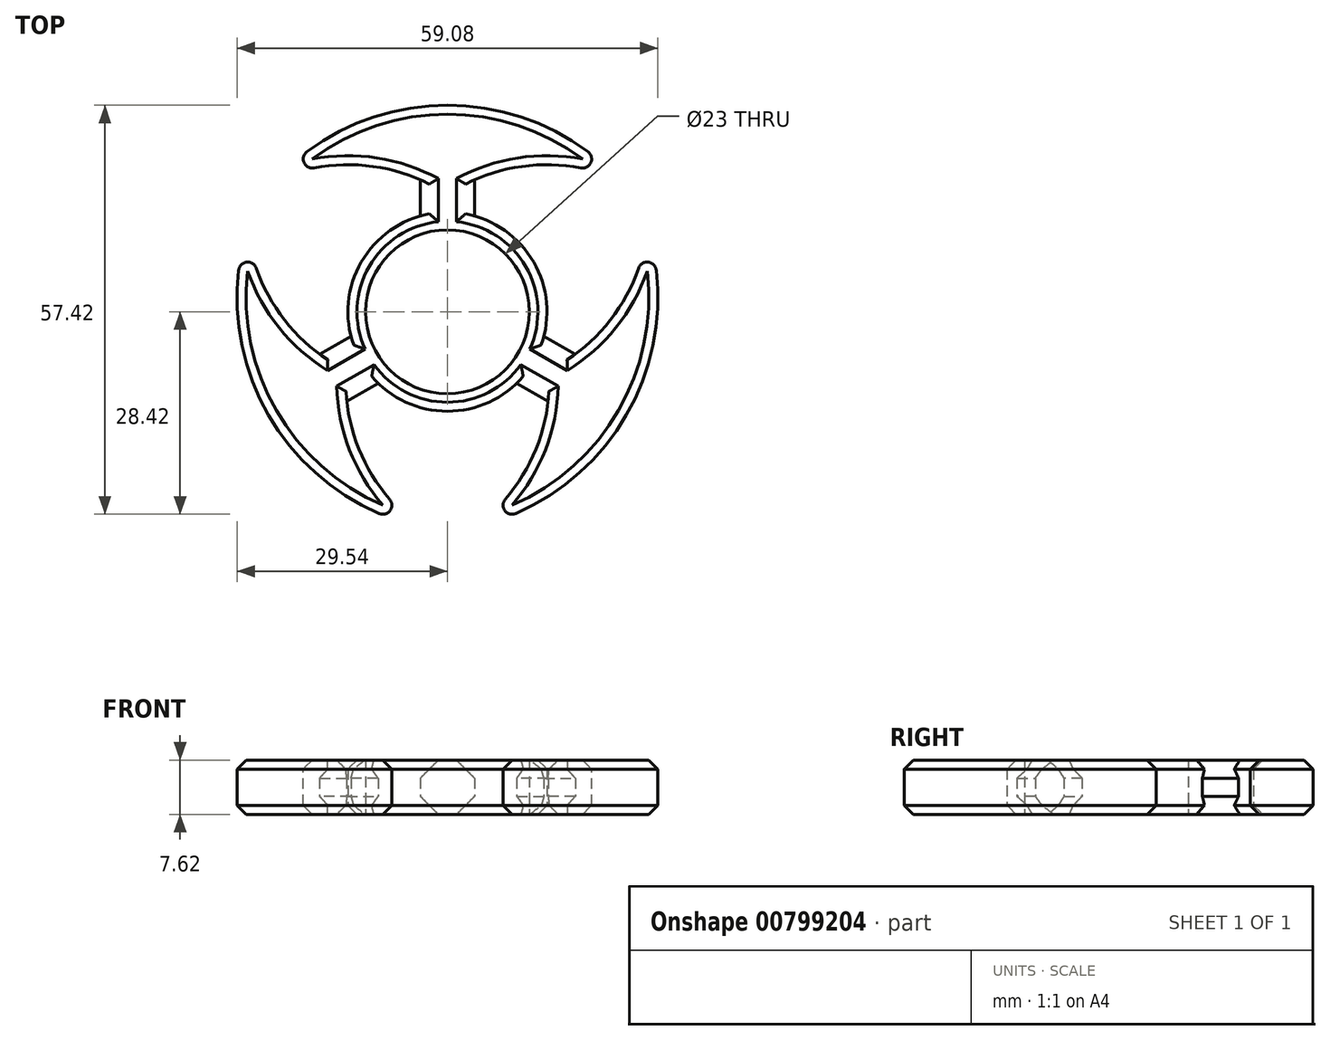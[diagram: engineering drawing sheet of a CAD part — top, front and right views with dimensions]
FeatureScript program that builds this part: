
annotation { "Feature Type Name" : "Feature", "Feature Type Description" : "" }
export const myFeature = defineFeature(function(context is Context, id is Id, definition is map)
    precondition{}
    {
        {
            var Q0;
            Q0=qCreatedBy(makeId("Top.planeOp"),FACE);
            var sketch = newSketch(context, id + "F0", { "sketchPlane" : qUnion([Q0])});
            skCircle(sketch, "E0", {"center": v(0, 0) * mm, "radius": 11.5 * mm});
            skCircle(sketch, "E1", {"center": v(0, 0) * mm, "radius": 13.97 * mm});
            skLineSegment(sketch, "E2", {"start": v(-3.8, 13.44) * mm, "end": v(-3.8, 18.52) * mm});
            skLineSegment(sketch, "E3", {"start": v(3.81, 13.44) * mm, "end": v(3.81, 18.52) * mm});
            skArc(sketch, "E4", {"start": v(-3.81, 18.52) * mm, "mid": v(-13.97, 20.64) * mm, "end": v(-24.13, 18.52) * mm});
            skArc(sketch, "E5", {"start": v(24.13, 18.52) * mm, "mid": v(13.97, 20.64) * mm, "end": v(3.8, 18.52) * mm});
            skArc(sketch, "E6", {"start": v(24.13, 18.52) * mm, "mid": v(0, 29) * mm, "end": v(-24.13, 18.52) * mm});
            skArc(sketch, "E7.1.0", {"start": v(-28.1, 11.64) * mm, "mid": v(-24.86, 1.78) * mm, "end": v(-17.94, -5.96) * mm});
            skArc(sketch, "E7.1.1", {"start": v(-14.13, -12.56) * mm, "mid": v(-10.9, -22.42) * mm, "end": v(-3.97, -30.16) * mm});
            skArc(sketch, "E7.1.2", {"start": v(-28.1, 11.64) * mm, "mid": v(-25.11, -14.5) * mm, "end": v(-3.97, -30.16) * mm});
            skLineSegment(sketch, "E7.1.3", {"start": v(-13.54, -3.42) * mm, "end": v(-17.94, -5.96) * mm});
            skLineSegment(sketch, "E7.1.4", {"start": v(-9.73, -10.02) * mm, "end": v(-14.13, -12.56) * mm});
            skArc(sketch, "E7.2.0", {"start": v(3.97, -30.16) * mm, "mid": v(10.9, -22.42) * mm, "end": v(14.13, -12.56) * mm});
            skArc(sketch, "E7.2.1", {"start": v(17.94, -5.96) * mm, "mid": v(24.86, 1.78) * mm, "end": v(28.1, 11.64) * mm});
            skArc(sketch, "E7.2.2", {"start": v(3.97, -30.16) * mm, "mid": v(25.11, -14.5) * mm, "end": v(28.1, 11.64) * mm});
            skLineSegment(sketch, "E7.2.3", {"start": v(9.73, -10.02) * mm, "end": v(14.13, -12.56) * mm});
            skLineSegment(sketch, "E7.2.4", {"start": v(13.54, -3.42) * mm, "end": v(17.94, -5.96) * mm});
            skSolve(sketch);
        }
        {
            var Q0;
            Q0=makeQuery(id+"F0.imprint","IMPRINT",FACE,{"disambiguationData":[TD([[makeQuery(id+"F0.imprint","IMPRINT",EDGE,{"derivedFrom":sQuery(id+"F0.wireOp",EDGE,"E0")}),-1.0]])]});
            var Q1;
            Q1=makeQuery(id+"F0.imprint","IMPRINT",FACE,{"disambiguationData":[TD([[makeQuery(id+"F0.imprint","IMPRINT",EDGE,{"derivedFrom":sQuery(id+"F0.wireOp",EDGE,"E7.1.0")}),-1.0]])]});
            var Q2;
            {var subQ1=sQuery(id+"F0.wireOp",EDGE,"E2");Q2=makeQuery(id+"F0.imprint","IMPRINT",FACE,{"disambiguationData":[TD([[makeQuery(id+"F0.imprint","IMPRINT",EDGE,{"derivedFrom":subQ1}),-1.0]])]});}
            var Q3;
            Q3=makeQuery(id+"F0.imprint","IMPRINT",FACE,{"disambiguationData":[TD([[makeQuery(id+"F0.imprint","IMPRINT",EDGE,{"derivedFrom":sQuery(id+"F0.wireOp",EDGE,"E7.2.0")}),-1.0]])]});
            extrude(context, id + "F1", {"entities" : qUnion([Q0, Q1, Q2, Q3]), "depth" : 7.62 * mm, "offsetDistance" : 25.4 * mm});
        }
        {
            var Q0;
            Q0=makeQuery(id+"F1.opExtrude","SWEPT_EDGE",EDGE,{"disambiguationData":[OSD([sQuery(id+"F0.wireOp",EDGE,"E7.1.1"),sQuery(id+"F0.wireOp",EDGE,"E7.1.2")])]});
            var Q1;
            Q1=makeQuery(id+"F1.opExtrude","SWEPT_EDGE",EDGE,{"disambiguationData":[OSD([sQuery(id+"F0.wireOp",EDGE,"E7.2.0"),sQuery(id+"F0.wireOp",EDGE,"E7.2.2")])]});
            var Q2;
            Q2=makeQuery(id+"F1.opExtrude","SWEPT_EDGE",EDGE,{"disambiguationData":[OSD([sQuery(id+"F0.wireOp",EDGE,"E7.2.1"),sQuery(id+"F0.wireOp",EDGE,"E7.2.2")])]});
            var Q3;
            Q3=makeQuery(id+"F1.opExtrude","SWEPT_EDGE",EDGE,{"disambiguationData":[OSD([sQuery(id+"F0.wireOp",EDGE,"E5"),sQuery(id+"F0.wireOp",EDGE,"E6")])]});
            var Q4;
            Q4=makeQuery(id+"F1.opExtrude","SWEPT_EDGE",EDGE,{"disambiguationData":[OSD([sQuery(id+"F0.wireOp",EDGE,"E4"),sQuery(id+"F0.wireOp",EDGE,"E6")])]});
            var Q5;
            Q5=makeQuery(id+"F1.opExtrude","SWEPT_EDGE",EDGE,{"disambiguationData":[OSD([sQuery(id+"F0.wireOp",EDGE,"E7.1.0"),sQuery(id+"F0.wireOp",EDGE,"E7.1.2")])]});
            fillet(context, id + "F2", {"entities" : qUnion([Q0, Q1, Q2, Q3, Q4, Q5]), "radius" : 1.27 * mm, "tangentPropagation" : true, "allowEdgeOverflow" : false});
        }
        {
            var Q0;
            Q0=makeQuery(id+"F1.opExtrude","CAP_EDGE",EDGE,{"disambiguationData":[OSD([sQuery(id+"F0.wireOp",EDGE,"E7.1.4")])],"isStart":false});
            var Q1;
            Q1=makeQuery(id+"F1.opExtrude","CAP_EDGE",EDGE,{"disambiguationData":[OSD([sQuery(id+"F0.wireOp",EDGE,"E7.1.3")])],"isStart":false});
            var Q2;
            Q2=makeQuery(id+"F1.opExtrude","CAP_EDGE",EDGE,{"disambiguationData":[OSD([sQuery(id+"F0.wireOp",EDGE,"E2")])],"isStart":false});
            var Q3;
            Q3=makeQuery(id+"F1.opExtrude","CAP_EDGE",EDGE,{"disambiguationData":[OSD([sQuery(id+"F0.wireOp",EDGE,"E3")])],"isStart":false});
            var Q4;
            Q4=makeQuery(id+"F1.opExtrude","CAP_EDGE",EDGE,{"disambiguationData":[OSD([sQuery(id+"F0.wireOp",EDGE,"E7.2.4")])],"isStart":false});
            var Q5;
            Q5=makeQuery(id+"F1.opExtrude","CAP_EDGE",EDGE,{"disambiguationData":[OSD([sQuery(id+"F0.wireOp",EDGE,"E7.2.3")])],"isStart":false});
            var Q6;
            Q6=makeQuery(id+"F1.opExtrude","CAP_EDGE",EDGE,{"disambiguationData":[OSD([sQuery(id+"F0.wireOp",EDGE,"E7.1.4")])],"isStart":true});
            var Q7;
            Q7=makeQuery(id+"F1.opExtrude","CAP_EDGE",EDGE,{"disambiguationData":[OSD([sQuery(id+"F0.wireOp",EDGE,"E7.1.3")])],"isStart":true});
            var Q8;
            Q8=makeQuery(id+"F1.opExtrude","CAP_EDGE",EDGE,{"disambiguationData":[OSD([sQuery(id+"F0.wireOp",EDGE,"E2")])],"isStart":true});
            var Q9;
            Q9=makeQuery(id+"F1.opExtrude","CAP_EDGE",EDGE,{"disambiguationData":[OSD([sQuery(id+"F0.wireOp",EDGE,"E3")])],"isStart":true});
            var Q10;
            Q10=makeQuery(id+"F1.opExtrude","CAP_EDGE",EDGE,{"disambiguationData":[OSD([sQuery(id+"F0.wireOp",EDGE,"E7.2.4")])],"isStart":true});
            var Q11;
            Q11=makeQuery(id+"F1.opExtrude","CAP_EDGE",EDGE,{"disambiguationData":[OSD([sQuery(id+"F0.wireOp",EDGE,"E7.2.3")])],"isStart":true});
            chamfer(context, id + "F3", {"entities" : qUnion([Q0, Q1, Q2, Q3, Q4, Q5, Q6, Q7, Q8, Q9, Q10, Q11]), "width" : 2.54 * mm, "tangentPropagation" : true});
        }
        {
            var Q0;
            Q0=makeQuery(id+"F1.opExtrude","CAP_EDGE",EDGE,{"disambiguationData":[OSD([sQuery(id+"F0.wireOp",EDGE,"E7.2.2")])],"isStart":true});
            var Q1;
            Q1=makeQuery(id+"F1.opExtrude","CAP_EDGE",EDGE,{"disambiguationData":[OSD([sQuery(id+"F0.wireOp",EDGE,"E6")])],"isStart":true});
            var Q2;
            Q2=makeQuery(id+"F1.opExtrude","CAP_EDGE",EDGE,{"disambiguationData":[OSD([sQuery(id+"F0.wireOp",EDGE,"E7.1.2")])],"isStart":true});
            var Q3;
            Q3=makeQuery(id+"F1.opExtrude","CAP_EDGE",EDGE,{"disambiguationData":[OSD([sQuery(id+"F0.wireOp",EDGE,"E7.2.2")])],"isStart":false});
            var Q4;
            Q4=makeQuery(id+"F1.opExtrude","CAP_EDGE",EDGE,{"disambiguationData":[OSD([sQuery(id+"F0.wireOp",EDGE,"E6")])],"isStart":false});
            var Q5;
            Q5=makeQuery(id+"F1.opExtrude","CAP_EDGE",EDGE,{"disambiguationData":[OSD([sQuery(id+"F0.wireOp",EDGE,"E7.1.2")])],"isStart":false});
            var Q6;
            {var subQ0=sQuery(id+"F0.wireOp",EDGE,"E1");Q6=makeQuery(id+"F1.opExtrude","CAP_EDGE",EDGE,{"disambiguationData":[OSD([subQ0]),TDD([makeQuery(id+"F0.imprint","IMPRINT",EDGE,{"disambiguationData":[TD([[makeQuery(id+"F0.imprint","INTERSECT",VERTEX,{"derivedFrom":[subQ0,sQuery(id+"F0.wireOp",EDGE,"E7.1.4")]}),-1.0]])],"derivedFrom":subQ0})])],"isStart":false});}
            var Q7;
            {var subQ0=sQuery(id+"F0.wireOp",EDGE,"E1");Q7=makeQuery(id+"F1.opExtrude","CAP_EDGE",EDGE,{"disambiguationData":[OSD([subQ0]),TDD([makeQuery(id+"F0.imprint","IMPRINT",EDGE,{"disambiguationData":[TD([[makeQuery(id+"F0.imprint","INTERSECT",VERTEX,{"derivedFrom":[subQ0,sQuery(id+"F0.wireOp",EDGE,"E3")]}),1.0]])],"derivedFrom":subQ0})])],"isStart":false});}
            var Q8;
            {var subQ0=sQuery(id+"F0.wireOp",EDGE,"E1");Q8=makeQuery(id+"F1.opExtrude","CAP_EDGE",EDGE,{"disambiguationData":[OSD([subQ0]),TDD([makeQuery(id+"F0.imprint","IMPRINT",EDGE,{"disambiguationData":[TD([[makeQuery(id+"F0.imprint","INTERSECT",VERTEX,{"derivedFrom":[subQ0,sQuery(id+"F0.wireOp",EDGE,"E2")]}),-1.0]])],"derivedFrom":subQ0})])],"isStart":false});}
            var Q9;
            {var subQ0=sQuery(id+"F0.wireOp",EDGE,"E1");Q9=makeQuery(id+"F1.opExtrude","CAP_EDGE",EDGE,{"disambiguationData":[OSD([subQ0]),TDD([makeQuery(id+"F0.imprint","IMPRINT",EDGE,{"disambiguationData":[TD([[makeQuery(id+"F0.imprint","INTERSECT",VERTEX,{"derivedFrom":[subQ0,sQuery(id+"F0.wireOp",EDGE,"E2")]}),-1.0]])],"derivedFrom":subQ0})])],"isStart":true});}
            var Q10;
            {var subQ0=sQuery(id+"F0.wireOp",EDGE,"E1");Q10=makeQuery(id+"F1.opExtrude","CAP_EDGE",EDGE,{"disambiguationData":[OSD([subQ0]),TDD([makeQuery(id+"F0.imprint","IMPRINT",EDGE,{"disambiguationData":[TD([[makeQuery(id+"F0.imprint","INTERSECT",VERTEX,{"derivedFrom":[subQ0,sQuery(id+"F0.wireOp",EDGE,"E7.1.4")]}),-1.0]])],"derivedFrom":subQ0})])],"isStart":true});}
            var Q11;
            {var subQ0=sQuery(id+"F0.wireOp",EDGE,"E1");Q11=makeQuery(id+"F1.opExtrude","CAP_EDGE",EDGE,{"disambiguationData":[OSD([subQ0]),TDD([makeQuery(id+"F0.imprint","IMPRINT",EDGE,{"disambiguationData":[TD([[makeQuery(id+"F0.imprint","INTERSECT",VERTEX,{"derivedFrom":[subQ0,sQuery(id+"F0.wireOp",EDGE,"E3")]}),1.0]])],"derivedFrom":subQ0})])],"isStart":true});}
            chamfer(context, id + "F4", {"entities" : qUnion([Q0, Q1, Q2, Q3, Q4, Q5, Q6, Q7, Q8, Q9, Q10, Q11]), "width" : 1.27 * mm, "tangentPropagation" : true});
        }
    });
